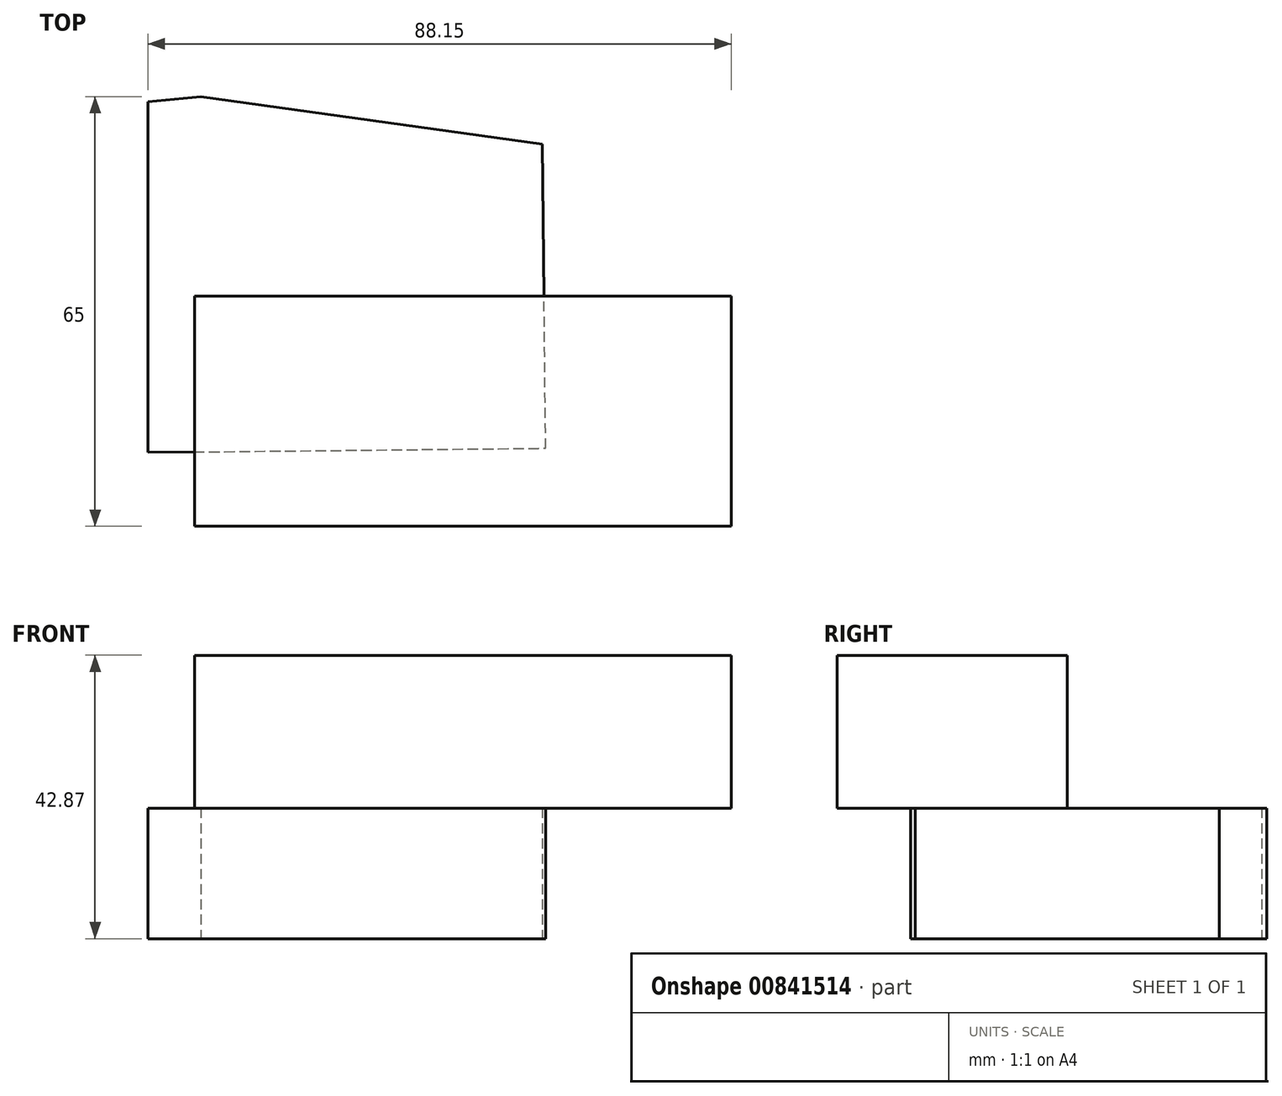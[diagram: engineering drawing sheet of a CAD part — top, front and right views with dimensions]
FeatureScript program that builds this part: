
annotation { "Feature Type Name" : "Feature", "Feature Type Description" : "" }
export const myFeature = defineFeature(function(context is Context, id is Id, definition is map)
    precondition{}
    {
        {
            var Q0;
            Q0=qCreatedBy(makeId("Top.planeOp"),FACE);
            var sketch = newSketch(context, id + "F0", { "sketchPlane" : qUnion([Q0])});
            skLineSegment(sketch, "E0", {"start": v(-24.18, 30.91) * mm, "end": v(-24.18, -25.77) * mm});
            skLineSegment(sketch, "E1", {"start": v(-24.18, -25.77) * mm, "end": v(35.93, -25.13) * mm});
            skLineSegment(sketch, "E2", {"start": v(35.93, -25.13) * mm, "end": v(35.43, 20.9) * mm});
            skLineSegment(sketch, "E3", {"start": v(35.43, 20.9) * mm, "end": v(-16.21, 28.06) * mm});
            skLineSegment(sketch, "E4", {"start": v(-16.21, 28.06) * mm, "end": v(-25.22, 27.2) * mm});
            skLineSegment(sketch, "E5", {"start": v(-25.22, 27.2) * mm, "end": v(-16.21, 28.06) * mm});
            skSolve(sketch);
        }
        {
            var Q0;
            {var subQ1=sQuery(id+"F0.wireOp",EDGE,"E1");Q0=makeQuery(id+"F0.imprint","IMPRINT",FACE,{"disambiguationData":[TD([[makeQuery(id+"F0.imprint","IMPRINT",EDGE,{"derivedFrom":subQ1}),1.0]])]});}
            extrude(context, id + "F1", {"entities" : qUnion([Q0]), "depth" : 19.73 * mm, "offsetDistance" : 25.4 * mm});
        }
        {
            var Q0;
            Q0=makeQuery(id+"F1.opExtrude","CAP_FACE",FACE,{"disambiguationData":[OSD([sQuery(id+"F0.wireOp",EDGE,"E0"),sQuery(id+"F0.wireOp",EDGE,"E1"),sQuery(id+"F0.wireOp",EDGE,"E2"),sQuery(id+"F0.wireOp",EDGE,"E3"),sQuery(id+"F0.wireOp",EDGE,"E5")])],"isStart":false});
            var sketch = newSketch(context, id + "F2", { "sketchPlane" : qUnion([Q0])});
            skPoint(sketch, "E6.oppositeSnap0", {"position": v(35.68, -2.12) * mm});
            skLineSegment(sketch, "E6.bottom", {"start": v(-17.16, -36.94) * mm, "end": v(63.97, -36.94) * mm});
            skLineSegment(sketch, "E6.top", {"start": v(-17.16, -2.12) * mm, "end": v(63.97, -2.12) * mm});
            skLineSegment(sketch, "E6.left", {"start": v(-17.16, -36.94) * mm, "end": v(-17.16, -2.12) * mm});
            skLineSegment(sketch, "E6.right", {"start": v(63.97, -36.94) * mm, "end": v(63.97, -2.12) * mm});
            skSolve(sketch);
        }
        {
            var Q0;
            {var subQ0=sQuery(id+"F2.wireOp",EDGE,"E6.left");var subQ1=sQuery(id+"F2.wireOp",EDGE,"E6.top");var subQ2=makeQuery(id+"F2.imprint","INTERSECT",VERTEX,{"derivedFrom":[subQ1,subQ0]});Q0=makeQuery(id+"F2.imprint","IMPRINT",FACE,{"disambiguationData":[TD([[makeQuery(id+"F2.imprint","IMPRINT",EDGE,{"disambiguationData":[TD([[subQ2,-1.0]])],"derivedFrom":subQ1}),-1.0]])]});}
            var Q1;
            {var subQ1=sQuery(id+"F2.wireOp",EDGE,"E6.bottom");Q1=makeQuery(id+"F2.imprint","IMPRINT",FACE,{"disambiguationData":[TD([[makeQuery(id+"F2.imprint","IMPRINT",EDGE,{"derivedFrom":subQ1}),1.0]])]});}
            extrude(context, id + "F3", {"entities" : qUnion([Q0, Q1]), "operationType" : NewBodyOperationType.ADD, "depth" : 23.14 * mm, "offsetDistance" : 25.4 * mm});
        }
    });
